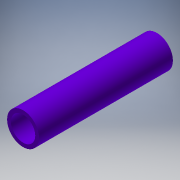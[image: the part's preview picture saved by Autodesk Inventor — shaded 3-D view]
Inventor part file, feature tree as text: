
AUTODESK INVENTOR PART (.ipt)
format: ipt  version: 2018.2 (Build 222227000, 227)  size: 109,568 bytes
history: native  units: in
note: dims shown in document units (in); Inventor stores cm internally (conversion verified against a paired STEP export)
features: extrude x1, sketch x1
ambient origin geometry x8: Origin, YZ Plane, XZ Plane, XY Plane, X Axis, Y Axis, Z Axis, Center Point
bodies: Solid1 (feature_tree)
feature tree (2):
  extrude  "Extrusion1"  Depth=5.5in
  sketch  "Sketch1"  dims[d0=1.315in d1=1.0in d2=5.5in d3=0.0in]
